# Revit family: Domotics-DomesticRanges-GEWISS-CHORUS_PROTECTION-ONE-WAY_SWITCH_RCBO
name_source: partatom
category: Apparecchi elettrici
revit_build: Autodesk Revit 2016 (Build: 20161004_0715(x64)
units: mm (PartAtom-declared; Revit-internal decimal feet)

## family parameters
Condiviso = Sì
Host = Superficie
Mantenere orientamento annotazione = Sì
Punto di calcolo locali = Sì
Quota connettore circolare = Usa diametro
Taglio con vuoti quando caricato = Sì
Tipo di parte = Normale

## types (18) — shared parameters
Breaking capacity = 3KA
Carico apparente = 0 VA
Catalogue = DOMOTICS
Catalogue Range = CHORUS - DOMESTIC RANGE
Curve = C
Description. = One-way switch (1P+N)
Description: = Two-pole (1P+N)
Electrocod = 0131
IDF = e0e07ccc-7455-4c48-8f2f-378de52475b4
IDT = 460529f6-09a6-4f16-8ae1-ce9d8c67e3d4
Immagine tipo = GW14482.jpg
N. poli = 1
No. Chorus modules = 2
No. Chorus modules: = 2
Produttore = GEWISS S.p.A.
Prospetto di default = 1219 mm
SEO = RCCB
Technical sheet = https://www.gewiss.com
Tipo_ = CHORUS INT MAGNETOT.DIFFERENZIALE_GENERALE : TITANIO
Type = Miniature circuit breaker + residual current device
Type: = A
URL = https://www.gewiss.com
Version file RFA = 19.0
Volt = 230 V
Voltage = 230V ac
Voltage: = 230V ac

## per-type parameters (varying)
| type | Colour | Descrizione | EAN code | Idn | Modello | Rated current (A) | Rated current (In) | Rated residual operating current |
| GW10486 - RCBO 1P+N C10 30ma 230V ac 3kA White | White | RCBO 1P+N C10 30mA 230V ac 3KA W. | 8011564262805 | 30MA | GW10486 | 10 | 10 | 30MA |
| GW12488 - RCBO 1P+N C16 10ma 230V ac 3kA Black | Black | RCBO 1P+N C16 10mA 230V ac 3KA B. | 8011564267893 | 10MA | GW12488 | 16 | 16 | 10MA |
| GW14486 - RCBO 1P+N C10 30ma 230V ac 3kA Titanium | Titanium | RCBO 1P+N C10 30mA 230V ac 3KA T. | 8011564267794 | 30MA | GW14486 | 10 | 10 | 30MA |
| GW10488 - RCBO 1P+N C16 10ma 230V ac 3kA White | White | RCBO 1P+N C16 10mA 230V ac 3KA W. | 8011564262812 | 10MA | GW10488 | 16 | 16 | 10MA |
| GW10485 - RCBO 1P+N C10 10ma 230V ac 3kA White | White | RCBO 1P+N C10 10mA 230V ac 3KA W. | 8011564262799 | 10MA | GW10485 | 10 | 10 | 10MA |
| GW14485 - RCBO 1P+N C10 10ma 230V ac 3kA Titanium | Titanium | RCBO 1P+N C10 10mA 230V ac 3KA T. | 8011564267787 | 10MA | GW14485 | 10 | 10 | 10MA |
| GW14489 - RCBO 1P+N C16 30ma 230V ac 3kA Titanium | Titanium | RCBO 1P+N C16 30mA 230V ac 3KA T. | 8011564267817 | 30MA | GW14489 | 16 | 16 | 30MA |
| GW12486 - RCBO 1P+N C10 30ma 230V ac 3kA Black | Black | RCBO 1P+N C10 30mA 230V ac 3KA B. | 8011564267886 | 30MA | GW12486 | 10 | 10 | 30MA |
| GW12483 - RCBO 1P+N C6 30ma 230V ac 3kA Black | Black | RCBO 1P+N C6 30mA 230V ac 3KA B. | 8011564265158 | 30MA | GW12483 | 6 | 6 | 30MA |
| GW12489 - RCBO 1P+N C16 30ma 230V ac 3kA Black | Black | RCBO 1P+N C16 30mA 230V ac 3KA B. | 8011564267916 | 30MA | GW12489 | 16 | 16 | 30MA |
| GW10483 - RCBO 1P+N C6 30ma 230V ac 3kA White | White | RCBO 1P+N C6 30mA 230V ac 3KA W. | 8011564262782 | 30MA | GW10483 | 6 | 6 | 30MA |
| GW14482 - RCBO 1P+N C6 10ma 230V ac 3kA Titanium | Titanium | RCBO 1P+N C6 10mA 230V ac 3KA T. | 8011564267763 | 10MA | GW14482 | 6 | 6 | 10MA |
| GW14488 - RCBO 1P+N C16 10ma 230V ac 3kA Titanium | Titanium | RCBO 1P+N C16 10mA 230V ac 3KA T. | 8011564267800 | 10MA | GW14488 | 16 | 16 | 10MA |
| GW12485 - RCBO 1P+N C10 10ma 230V ac 3kA Black | Black | RCBO 1P+N C10 10mA 230V ac 3KA B. | 8011564265165 | 10MA | GW12485 | 10 | 10 | 10MA |
| GW12482 - RCBO 1P+N C6 10ma 230V ac 3kA Black | Black | RCBO 1P+N C6 10mA 230V ac 3KA B. | 8011564265141 | 10MA | GW12482 | 6 | 6 | 10MA |
| GW10482 - RCBO 1P+N C6 10ma 230V ac 3kA White | White | RCBO 1P+N C6 10mA 230V ac 3KA W. | 8011564262775 | 10MA | GW10482 | 6 | 6 | 10MA |
| GW14483 - RCBO 1P+N C6 30ma 230V ac 3kA Titanium | Titanium | RCBO 1P+N C6 30mA 230V ac 3KA T. | 8011564267770 | 30MA | GW14483 | 6 | 6 | 30MA |
| GW10489 - RCBO 1P+N C16 30ma 230V ac 3kA White | White | RCBO 1P+N C16 30mA 230V ac 3KA W. | 8011564262829 | 30MA | GW10489 | 16 | 16 | 30MA |

## geometry (parser evidence)
native form markers: Sweep x2
no freeform markers — native parametric forms only
